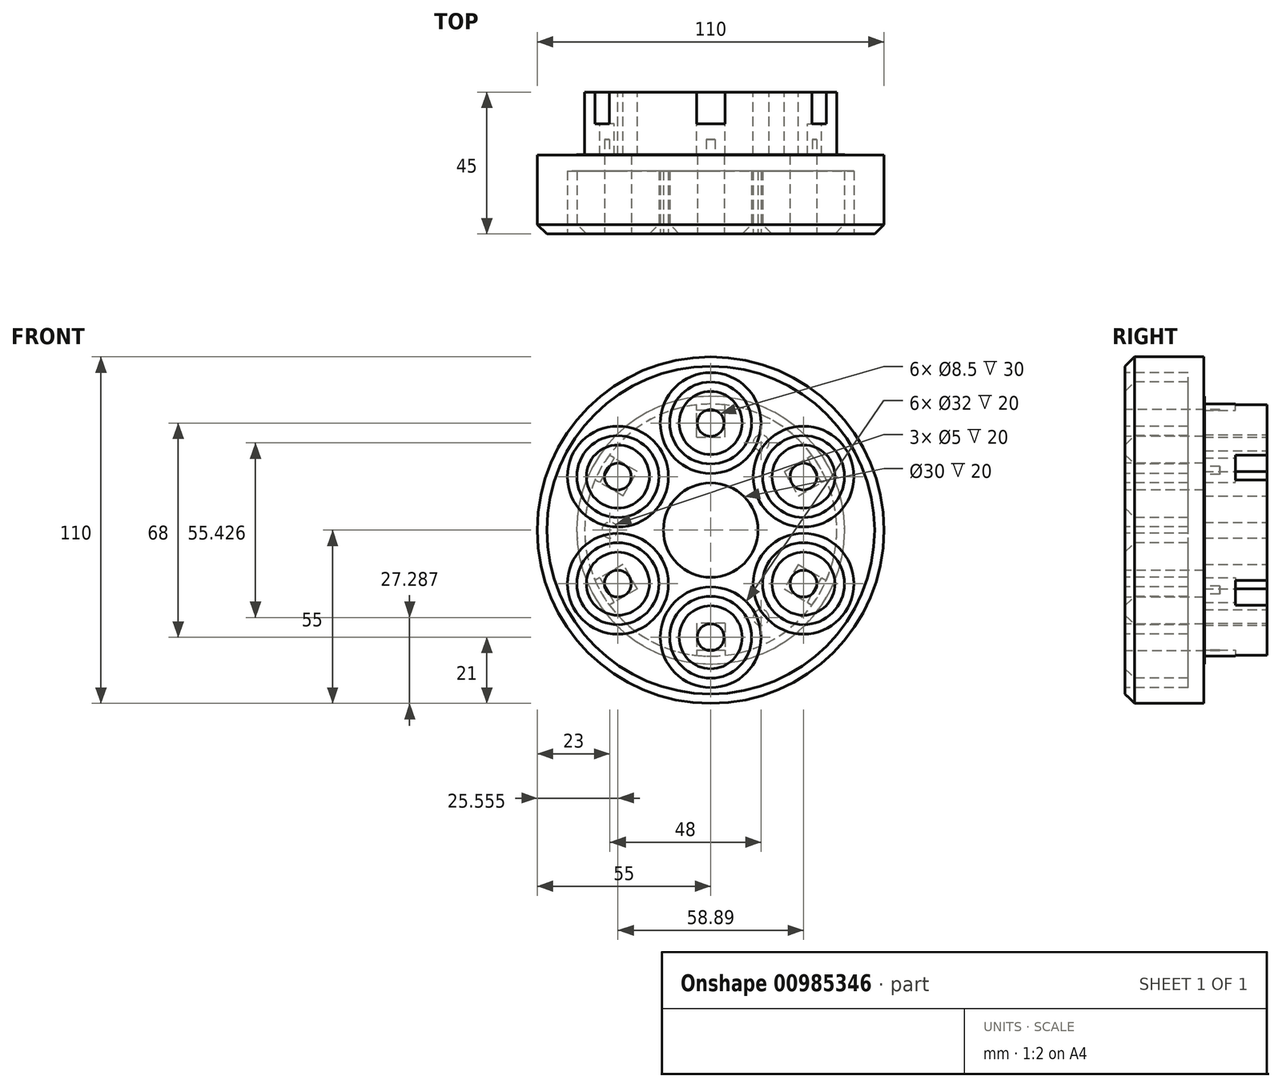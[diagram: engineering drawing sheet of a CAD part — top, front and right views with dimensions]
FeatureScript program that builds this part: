
annotation { "Feature Type Name" : "Feature", "Feature Type Description" : "" }
export const myFeature = defineFeature(function(context is Context, id is Id, definition is map)
    precondition{}
    {
        {
            var Q0;
            Q0=qCreatedBy(makeId("Front.planeOp"),FACE);
            var sketch = newSketch(context, id + "F0", { "sketchPlane" : qUnion([Q0])});
            skCircle(sketch, "E0", {"center": v(0, 0) * mm, "radius": 40 * mm});
            skCircle(sketch, "E1", {"center": v(0, 34) * mm, "radius": 3.25 * mm});
            skCircle(sketch, "E2.1.0", {"center": v(-29.44, 17) * mm, "radius": 3.25 * mm});
            skCircle(sketch, "E2.2.0", {"center": v(-29.44, -17) * mm, "radius": 3.25 * mm});
            skCircle(sketch, "E2.3.0", {"center": v(0, -34) * mm, "radius": 3.25 * mm});
            skCircle(sketch, "E2.4.0", {"center": v(29.44, -17) * mm, "radius": 3.25 * mm});
            skCircle(sketch, "E2.5.0", {"center": v(29.44, 17) * mm, "radius": 3.25 * mm});
            skSolve(sketch);
        }
        {
            var Q0;
            Q0=qSketchRegion(id+"F0",true);
            extrude(context, id + "F1", {"entities" : qUnion([Q0]), "depth" : 45 * mm});
        }
        {
            var Q0;
            Q0=makeQuery(id+"F1.opExtrude","CAP_FACE",FACE,{"disambiguationData":[OSD([sQuery(id+"F0.wireOp",EDGE,"E0"),sQuery(id+"F0.wireOp",EDGE,"E1"),sQuery(id+"F0.wireOp",EDGE,"E2.1.0"),sQuery(id+"F0.wireOp",EDGE,"E2.2.0"),sQuery(id+"F0.wireOp",EDGE,"E2.3.0"),sQuery(id+"F0.wireOp",EDGE,"E2.4.0"),sQuery(id+"F0.wireOp",EDGE,"E2.5.0")])],"isStart":false});
            var sketch = newSketch(context, id + "F2", { "sketchPlane" : qUnion([Q0])});
            skCircle(sketch, "E3", {"center": v(0, 34) * mm, "radius": 4.25 * mm});
            skCircle(sketch, "E4.1.0", {"center": v(-29.44, 17) * mm, "radius": 4.25 * mm});
            skCircle(sketch, "E4.2.0", {"center": v(-29.44, -17) * mm, "radius": 4.25 * mm});
            skCircle(sketch, "E4.3.0", {"center": v(0, -34) * mm, "radius": 4.25 * mm});
            skCircle(sketch, "E4.4.0", {"center": v(29.44, -17) * mm, "radius": 4.25 * mm});
            skCircle(sketch, "E4.5.0", {"center": v(29.44, 17) * mm, "radius": 4.25 * mm});
            skPoint(sketch, "E4.center", {"position": v(0, 0) * mm});
            skSolve(sketch);
        }
        {
            var Q0;
            Q0=qSketchRegion(id+"F2",true);
            extrude(context, id + "F3", {"entities" : qUnion([Q0]), "operationType" : NewBodyOperationType.REMOVE, "oppositeDirection" : true, "depth" : 30 * mm});
        }
        {
            var Q0;
            Q0=makeQuery(id+"F1.opExtrude","CAP_FACE",FACE,{"disambiguationData":[OSD([sQuery(id+"F0.wireOp",EDGE,"E0"),sQuery(id+"F0.wireOp",EDGE,"E1"),sQuery(id+"F0.wireOp",EDGE,"E2.1.0"),sQuery(id+"F0.wireOp",EDGE,"E2.2.0"),sQuery(id+"F0.wireOp",EDGE,"E2.3.0"),sQuery(id+"F0.wireOp",EDGE,"E2.4.0"),sQuery(id+"F0.wireOp",EDGE,"E2.5.0")])],"isStart":true});
            var sketch = newSketch(context, id + "F4", { "sketchPlane" : qUnion([Q0])});
            skCircle(sketch, "E5", {"center": v(0, 34) * mm, "radius": 4.5 * mm});
            skCircle(sketch, "E6.1.0", {"center": v(-29.44, 17) * mm, "radius": 4.5 * mm});
            skCircle(sketch, "E6.2.0", {"center": v(-29.44, -17) * mm, "radius": 4.5 * mm});
            skCircle(sketch, "E6.3.0", {"center": v(0, -34) * mm, "radius": 4.5 * mm});
            skCircle(sketch, "E6.4.0", {"center": v(29.44, -17) * mm, "radius": 4.5 * mm});
            skCircle(sketch, "E6.5.0", {"center": v(29.44, 17) * mm, "radius": 4.5 * mm});
            skPoint(sketch, "E6.center", {"position": v(0, 0) * mm});
            skCircle(sketch, "E7", {"center": v(32, 0) * mm, "radius": 2.5 * mm});
            skCircle(sketch, "E8.1.0", {"center": v(-16, 27.71) * mm, "radius": 2.5 * mm});
            skCircle(sketch, "E8.2.0", {"center": v(-16, -27.71) * mm, "radius": 2.5 * mm});
            skSolve(sketch);
        }
        {
            var Q0;
            Q0=makeQuery(id+"F4.imprint","IMPRINT",FACE,{"disambiguationData":[TD([[makeQuery(id+"F4.imprint","IMPRINT",EDGE,{"derivedFrom":sQuery(id+"F4.wireOp",EDGE,"E8.1.0")}),1.0]])]});
            var Q1;
            Q1=makeQuery(id+"F4.imprint","IMPRINT",FACE,{"disambiguationData":[TD([[makeQuery(id+"F4.imprint","IMPRINT",EDGE,{"derivedFrom":sQuery(id+"F4.wireOp",EDGE,"E7")}),1.0]])]});
            var Q2;
            Q2=makeQuery(id+"F4.imprint","IMPRINT",FACE,{"disambiguationData":[TD([[makeQuery(id+"F4.imprint","IMPRINT",EDGE,{"derivedFrom":sQuery(id+"F4.wireOp",EDGE,"E8.2.0")}),1.0]])]});
            extrude(context, id + "F5", {"entities" : qUnion([Q0, Q1, Q2]), "operationType" : NewBodyOperationType.REMOVE, "oppositeDirection" : true, "depth" : 20 * mm});
        }
        {
            var Q0;
            Q0=makeQuery(id+"F1.opExtrude","CAP_FACE",FACE,{"disambiguationData":[OSD([sQuery(id+"F0.wireOp",EDGE,"E0"),sQuery(id+"F0.wireOp",EDGE,"E1"),sQuery(id+"F0.wireOp",EDGE,"E2.1.0"),sQuery(id+"F0.wireOp",EDGE,"E2.2.0"),sQuery(id+"F0.wireOp",EDGE,"E2.3.0"),sQuery(id+"F0.wireOp",EDGE,"E2.4.0"),sQuery(id+"F0.wireOp",EDGE,"E2.5.0")])],"isStart":false});
            var sketch = newSketch(context, id + "F6", { "sketchPlane" : qUnion([Q0])});
            skCircle(sketch, "E9", {"center": v(0, 0) * mm, "radius": 55 * mm});
            skCircle(sketch, "E10", {"center": v(0, 34) * mm, "radius": 16 * mm});
            skCircle(sketch, "E11.1.0", {"center": v(-29.44, 17) * mm, "radius": 16 * mm});
            skCircle(sketch, "E11.2.0", {"center": v(-29.44, -17) * mm, "radius": 16 * mm});
            skCircle(sketch, "E11.3.0", {"center": v(0, -34) * mm, "radius": 16 * mm});
            skCircle(sketch, "E11.4.0", {"center": v(29.44, -17) * mm, "radius": 16 * mm});
            skCircle(sketch, "E11.5.0", {"center": v(29.44, 17) * mm, "radius": 16 * mm});
            skCircle(sketch, "E12", {"center": v(0, 0) * mm, "radius": 15 * mm});
            skCircle(sketch, "E13", {"center": v(0, -34) * mm, "radius": 13 * mm});
            skCircle(sketch, "E14.1.0", {"center": v(29.44, -17) * mm, "radius": 13 * mm});
            skCircle(sketch, "E14.2.0", {"center": v(29.44, 17) * mm, "radius": 13 * mm});
            skCircle(sketch, "E14.3.0", {"center": v(0, 34) * mm, "radius": 13 * mm});
            skCircle(sketch, "E14.4.0", {"center": v(-29.44, 17) * mm, "radius": 13 * mm});
            skCircle(sketch, "E14.5.0", {"center": v(-29.44, -17) * mm, "radius": 13 * mm});
            skSolve(sketch);
        }
        {
            var Q0;
            Q0=makeQuery(id+"F6.imprint","IMPRINT",FACE,{"disambiguationData":[TD([[makeQuery(id+"F6.imprint","IMPRINT",EDGE,{"derivedFrom":sQuery(id+"F6.wireOp",EDGE,"E9")}),1.0]])]});
            var Q1;
            {var subQ0=sQuery(id+"F6.wireOp",EDGE,"E11.1.0");var subQ1=makeQuery(id+"F1.opExtrude","CAP_EDGE",EDGE,{"disambiguationData":[OSD([sQuery(id+"F0.wireOp",EDGE,"E0")])],"isStart":false});var subQ2=makeQuery(id+"F6.imprint","INTERSECT",VERTEX,{"disambiguationData":[OD(0.0)],"derivedFrom":[subQ1,subQ0]});Q1=makeQuery(id+"F6.imprint","IMPRINT",FACE,{"disambiguationData":[TD([[makeQuery(id+"F6.imprint","IMPRINT",EDGE,{"disambiguationData":[TD([[subQ2,1.0]])],"derivedFrom":subQ0}),1.0]])]});}
            var Q2;
            {var subQ0=sQuery(id+"F6.wireOp",EDGE,"E10");var subQ1=makeQuery(id+"F1.opExtrude","CAP_EDGE",EDGE,{"disambiguationData":[OSD([sQuery(id+"F0.wireOp",EDGE,"E0")])],"isStart":false});var subQ2=makeQuery(id+"F6.imprint","INTERSECT",VERTEX,{"disambiguationData":[OD(0.0)],"derivedFrom":[subQ1,subQ0]});Q2=makeQuery(id+"F6.imprint","IMPRINT",FACE,{"disambiguationData":[TD([[makeQuery(id+"F6.imprint","IMPRINT",EDGE,{"disambiguationData":[TD([[subQ2,1.0]])],"derivedFrom":subQ0}),1.0]])]});}
            var Q3;
            {var subQ0=sQuery(id+"F6.wireOp",EDGE,"E11.5.0");var subQ1=makeQuery(id+"F1.opExtrude","CAP_EDGE",EDGE,{"disambiguationData":[OSD([sQuery(id+"F0.wireOp",EDGE,"E0")])],"isStart":false});var subQ2=makeQuery(id+"F6.imprint","INTERSECT",VERTEX,{"disambiguationData":[OD(0.0)],"derivedFrom":[subQ1,subQ0]});Q3=makeQuery(id+"F6.imprint","IMPRINT",FACE,{"disambiguationData":[TD([[makeQuery(id+"F6.imprint","IMPRINT",EDGE,{"disambiguationData":[TD([[subQ2,1.0]])],"derivedFrom":subQ0}),1.0]])]});}
            var Q4;
            {var subQ0=sQuery(id+"F6.wireOp",EDGE,"E11.2.0");var subQ1=makeQuery(id+"F1.opExtrude","CAP_EDGE",EDGE,{"disambiguationData":[OSD([sQuery(id+"F0.wireOp",EDGE,"E0")])],"isStart":false});var subQ2=makeQuery(id+"F6.imprint","INTERSECT",VERTEX,{"disambiguationData":[OD(0.0)],"derivedFrom":[subQ1,subQ0]});Q4=makeQuery(id+"F6.imprint","IMPRINT",FACE,{"disambiguationData":[TD([[makeQuery(id+"F6.imprint","IMPRINT",EDGE,{"disambiguationData":[TD([[subQ2,-1.0]])],"derivedFrom":subQ0}),1.0]])]});}
            var Q5;
            {var subQ0=sQuery(id+"F6.wireOp",EDGE,"E11.3.0");var subQ1=makeQuery(id+"F1.opExtrude","CAP_EDGE",EDGE,{"disambiguationData":[OSD([sQuery(id+"F0.wireOp",EDGE,"E0")])],"isStart":false});var subQ2=makeQuery(id+"F6.imprint","INTERSECT",VERTEX,{"disambiguationData":[OD(0.0)],"derivedFrom":[subQ1,subQ0]});Q5=makeQuery(id+"F6.imprint","IMPRINT",FACE,{"disambiguationData":[TD([[makeQuery(id+"F6.imprint","IMPRINT",EDGE,{"disambiguationData":[TD([[subQ2,-1.0]])],"derivedFrom":subQ0}),1.0]])]});}
            var Q6;
            {var subQ0=sQuery(id+"F6.wireOp",EDGE,"E11.4.0");var subQ1=makeQuery(id+"F1.opExtrude","CAP_EDGE",EDGE,{"disambiguationData":[OSD([sQuery(id+"F0.wireOp",EDGE,"E0")])],"isStart":false});var subQ2=makeQuery(id+"F6.imprint","INTERSECT",VERTEX,{"disambiguationData":[OD(0.0)],"derivedFrom":[subQ1,subQ0]});Q6=makeQuery(id+"F6.imprint","IMPRINT",FACE,{"disambiguationData":[TD([[makeQuery(id+"F6.imprint","IMPRINT",EDGE,{"disambiguationData":[TD([[subQ2,-1.0]])],"derivedFrom":subQ0}),1.0]])]});}
            var Q7;
            {var subQ0=sQuery(id+"F6.wireOp",EDGE,"E14.5.0");var subQ1=makeQuery(id+"F1.opExtrude","CAP_EDGE",EDGE,{"disambiguationData":[OSD([sQuery(id+"F0.wireOp",EDGE,"E0")])],"isStart":false});var subQ2=makeQuery(id+"F6.imprint","INTERSECT",VERTEX,{"disambiguationData":[OD(0.0)],"derivedFrom":[subQ1,subQ0]});Q7=makeQuery(id+"F6.imprint","IMPRINT",FACE,{"disambiguationData":[TD([[makeQuery(id+"F6.imprint","IMPRINT",EDGE,{"disambiguationData":[TD([[subQ2,-1.0]])],"derivedFrom":subQ0}),1.0]])]});}
            var Q8;
            {var subQ0=sQuery(id+"F6.wireOp",EDGE,"E14.4.0");var subQ1=makeQuery(id+"F1.opExtrude","CAP_EDGE",EDGE,{"disambiguationData":[OSD([sQuery(id+"F0.wireOp",EDGE,"E0")])],"isStart":false});var subQ2=makeQuery(id+"F6.imprint","INTERSECT",VERTEX,{"disambiguationData":[OD(0.0)],"derivedFrom":[subQ1,subQ0]});Q8=makeQuery(id+"F6.imprint","IMPRINT",FACE,{"disambiguationData":[TD([[makeQuery(id+"F6.imprint","IMPRINT",EDGE,{"disambiguationData":[TD([[subQ2,1.0]])],"derivedFrom":subQ0}),1.0]])]});}
            var Q9;
            {var subQ0=sQuery(id+"F6.wireOp",EDGE,"E14.3.0");var subQ1=makeQuery(id+"F1.opExtrude","CAP_EDGE",EDGE,{"disambiguationData":[OSD([sQuery(id+"F0.wireOp",EDGE,"E0")])],"isStart":false});var subQ2=makeQuery(id+"F6.imprint","INTERSECT",VERTEX,{"disambiguationData":[OD(0.0)],"derivedFrom":[subQ1,subQ0]});Q9=makeQuery(id+"F6.imprint","IMPRINT",FACE,{"disambiguationData":[TD([[makeQuery(id+"F6.imprint","IMPRINT",EDGE,{"disambiguationData":[TD([[subQ2,1.0]])],"derivedFrom":subQ0}),1.0]])]});}
            var Q10;
            {var subQ0=sQuery(id+"F6.wireOp",EDGE,"E14.2.0");var subQ1=makeQuery(id+"F1.opExtrude","CAP_EDGE",EDGE,{"disambiguationData":[OSD([sQuery(id+"F0.wireOp",EDGE,"E0")])],"isStart":false});var subQ2=makeQuery(id+"F6.imprint","INTERSECT",VERTEX,{"disambiguationData":[OD(0.0)],"derivedFrom":[subQ1,subQ0]});Q10=makeQuery(id+"F6.imprint","IMPRINT",FACE,{"disambiguationData":[TD([[makeQuery(id+"F6.imprint","IMPRINT",EDGE,{"disambiguationData":[TD([[subQ2,1.0]])],"derivedFrom":subQ0}),1.0]])]});}
            var Q11;
            {var subQ0=sQuery(id+"F6.wireOp",EDGE,"E14.1.0");var subQ1=makeQuery(id+"F1.opExtrude","CAP_EDGE",EDGE,{"disambiguationData":[OSD([sQuery(id+"F0.wireOp",EDGE,"E0")])],"isStart":false});var subQ2=makeQuery(id+"F6.imprint","INTERSECT",VERTEX,{"disambiguationData":[OD(0.0)],"derivedFrom":[subQ1,subQ0]});Q11=makeQuery(id+"F6.imprint","IMPRINT",FACE,{"disambiguationData":[TD([[makeQuery(id+"F6.imprint","IMPRINT",EDGE,{"disambiguationData":[TD([[subQ2,-1.0]])],"derivedFrom":subQ0}),1.0]])]});}
            var Q12;
            {var subQ0=sQuery(id+"F6.wireOp",EDGE,"E13");var subQ1=makeQuery(id+"F1.opExtrude","CAP_EDGE",EDGE,{"disambiguationData":[OSD([sQuery(id+"F0.wireOp",EDGE,"E0")])],"isStart":false});var subQ2=makeQuery(id+"F6.imprint","INTERSECT",VERTEX,{"disambiguationData":[OD(0.0)],"derivedFrom":[subQ1,subQ0]});Q12=makeQuery(id+"F6.imprint","IMPRINT",FACE,{"disambiguationData":[TD([[makeQuery(id+"F6.imprint","IMPRINT",EDGE,{"disambiguationData":[TD([[subQ2,-1.0]])],"derivedFrom":subQ0}),1.0]])]});}
            extrude(context, id + "F7", {"entities" : qUnion([Q0, Q1, Q2, Q3, Q4, Q5, Q6, Q7, Q8, Q9, Q10, Q11, Q12]), "operationType" : NewBodyOperationType.ADD, "oppositeDirection" : true, "depth" : 25 * mm});
        }
        {
            var Q0;
            {var subQ0=sQuery(id+"F6.wireOp",EDGE,"E11.3.0");var subQ1=makeQuery(id+"F1.opExtrude","CAP_EDGE",EDGE,{"disambiguationData":[OSD([sQuery(id+"F0.wireOp",EDGE,"E0")])],"isStart":false});var subQ2=makeQuery(id+"F6.imprint","INTERSECT",VERTEX,{"disambiguationData":[OD(0.0)],"derivedFrom":[subQ1,subQ0]});Q0=makeQuery(id+"F6.imprint","IMPRINT",FACE,{"disambiguationData":[TD([[makeQuery(id+"F6.imprint","IMPRINT",EDGE,{"disambiguationData":[TD([[subQ2,-1.0]])],"derivedFrom":subQ0}),1.0]])]});}
            var Q1;
            {var subQ0=sQuery(id+"F6.wireOp",EDGE,"E11.4.0");var subQ1=makeQuery(id+"F1.opExtrude","CAP_EDGE",EDGE,{"disambiguationData":[OSD([sQuery(id+"F0.wireOp",EDGE,"E0")])],"isStart":false});var subQ2=makeQuery(id+"F6.imprint","INTERSECT",VERTEX,{"disambiguationData":[OD(0.0)],"derivedFrom":[subQ1,subQ0]});Q1=makeQuery(id+"F6.imprint","IMPRINT",FACE,{"disambiguationData":[TD([[makeQuery(id+"F6.imprint","IMPRINT",EDGE,{"disambiguationData":[TD([[subQ2,-1.0]])],"derivedFrom":subQ0}),1.0]])]});}
            var Q2;
            {var subQ0=sQuery(id+"F6.wireOp",EDGE,"E11.5.0");var subQ1=makeQuery(id+"F1.opExtrude","CAP_EDGE",EDGE,{"disambiguationData":[OSD([sQuery(id+"F0.wireOp",EDGE,"E0")])],"isStart":false});var subQ2=makeQuery(id+"F6.imprint","INTERSECT",VERTEX,{"disambiguationData":[OD(0.0)],"derivedFrom":[subQ1,subQ0]});Q2=makeQuery(id+"F6.imprint","IMPRINT",FACE,{"disambiguationData":[TD([[makeQuery(id+"F6.imprint","IMPRINT",EDGE,{"disambiguationData":[TD([[subQ2,1.0]])],"derivedFrom":subQ0}),1.0]])]});}
            var Q3;
            {var subQ0=sQuery(id+"F6.wireOp",EDGE,"E11.1.0");var subQ1=makeQuery(id+"F1.opExtrude","CAP_EDGE",EDGE,{"disambiguationData":[OSD([sQuery(id+"F0.wireOp",EDGE,"E0")])],"isStart":false});var subQ2=makeQuery(id+"F6.imprint","INTERSECT",VERTEX,{"disambiguationData":[OD(0.0)],"derivedFrom":[subQ1,subQ0]});Q3=makeQuery(id+"F6.imprint","IMPRINT",FACE,{"disambiguationData":[TD([[makeQuery(id+"F6.imprint","IMPRINT",EDGE,{"disambiguationData":[TD([[subQ2,1.0]])],"derivedFrom":subQ0}),1.0]])]});}
            var Q4;
            {var subQ0=sQuery(id+"F6.wireOp",EDGE,"E10");var subQ1=makeQuery(id+"F1.opExtrude","CAP_EDGE",EDGE,{"disambiguationData":[OSD([sQuery(id+"F0.wireOp",EDGE,"E0")])],"isStart":false});var subQ2=makeQuery(id+"F6.imprint","INTERSECT",VERTEX,{"disambiguationData":[OD(0.0)],"derivedFrom":[subQ1,subQ0]});Q4=makeQuery(id+"F6.imprint","IMPRINT",FACE,{"disambiguationData":[TD([[makeQuery(id+"F6.imprint","IMPRINT",EDGE,{"disambiguationData":[TD([[subQ2,1.0]])],"derivedFrom":subQ0}),1.0]])]});}
            var Q5;
            Q5=makeQuery(id+"F6.imprint","IMPRINT",FACE,{"disambiguationData":[TD([[makeQuery(id+"F6.imprint","IMPRINT",EDGE,{"derivedFrom":sQuery(id+"F6.wireOp",EDGE,"E12")}),1.0]])]});
            var Q6;
            {var subQ0=sQuery(id+"F6.wireOp",EDGE,"E11.1.0");var subQ1=makeQuery(id+"F1.opExtrude","CAP_EDGE",EDGE,{"disambiguationData":[OSD([sQuery(id+"F0.wireOp",EDGE,"E0")])],"isStart":false});var subQ2=makeQuery(id+"F6.imprint","INTERSECT",VERTEX,{"disambiguationData":[OD(0.0)],"derivedFrom":[subQ1,subQ0]});Q6=makeQuery(id+"F6.imprint","IMPRINT",FACE,{"disambiguationData":[TD([[makeQuery(id+"F6.imprint","IMPRINT",EDGE,{"disambiguationData":[TD([[subQ2,-1.0]])],"derivedFrom":subQ0}),1.0]])]});}
            var Q7;
            {var subQ0=sQuery(id+"F6.wireOp",EDGE,"E11.2.0");var subQ1=makeQuery(id+"F1.opExtrude","CAP_EDGE",EDGE,{"disambiguationData":[OSD([sQuery(id+"F0.wireOp",EDGE,"E0")])],"isStart":false});var subQ2=makeQuery(id+"F6.imprint","INTERSECT",VERTEX,{"disambiguationData":[OD(0.0)],"derivedFrom":[subQ1,subQ0]});Q7=makeQuery(id+"F6.imprint","IMPRINT",FACE,{"disambiguationData":[TD([[makeQuery(id+"F6.imprint","IMPRINT",EDGE,{"disambiguationData":[TD([[subQ2,1.0]])],"derivedFrom":subQ0}),1.0]])]});}
            var Q8;
            {var subQ0=sQuery(id+"F6.wireOp",EDGE,"E11.2.0");var subQ1=makeQuery(id+"F1.opExtrude","CAP_EDGE",EDGE,{"disambiguationData":[OSD([sQuery(id+"F0.wireOp",EDGE,"E0")])],"isStart":false});var subQ2=makeQuery(id+"F6.imprint","INTERSECT",VERTEX,{"disambiguationData":[OD(0.0)],"derivedFrom":[subQ1,subQ0]});Q8=makeQuery(id+"F6.imprint","IMPRINT",FACE,{"disambiguationData":[TD([[makeQuery(id+"F6.imprint","IMPRINT",EDGE,{"disambiguationData":[TD([[subQ2,-1.0]])],"derivedFrom":subQ0}),1.0]])]});}
            var Q9;
            {var subQ0=sQuery(id+"F6.wireOp",EDGE,"E10");var subQ1=makeQuery(id+"F1.opExtrude","CAP_EDGE",EDGE,{"disambiguationData":[OSD([sQuery(id+"F0.wireOp",EDGE,"E0")])],"isStart":false});var subQ2=makeQuery(id+"F6.imprint","INTERSECT",VERTEX,{"disambiguationData":[OD(0.0)],"derivedFrom":[subQ1,subQ0]});Q9=makeQuery(id+"F6.imprint","IMPRINT",FACE,{"disambiguationData":[TD([[makeQuery(id+"F6.imprint","IMPRINT",EDGE,{"disambiguationData":[TD([[subQ2,-1.0]])],"derivedFrom":subQ0}),1.0]])]});}
            var Q10;
            {var subQ0=sQuery(id+"F6.wireOp",EDGE,"E11.5.0");var subQ1=makeQuery(id+"F1.opExtrude","CAP_EDGE",EDGE,{"disambiguationData":[OSD([sQuery(id+"F0.wireOp",EDGE,"E0")])],"isStart":false});var subQ2=makeQuery(id+"F6.imprint","INTERSECT",VERTEX,{"disambiguationData":[OD(0.0)],"derivedFrom":[subQ1,subQ0]});Q10=makeQuery(id+"F6.imprint","IMPRINT",FACE,{"disambiguationData":[TD([[makeQuery(id+"F6.imprint","IMPRINT",EDGE,{"disambiguationData":[TD([[subQ2,-1.0]])],"derivedFrom":subQ0}),1.0]])]});}
            var Q11;
            {var subQ0=sQuery(id+"F6.wireOp",EDGE,"E11.4.0");var subQ1=makeQuery(id+"F1.opExtrude","CAP_EDGE",EDGE,{"disambiguationData":[OSD([sQuery(id+"F0.wireOp",EDGE,"E0")])],"isStart":false});var subQ2=makeQuery(id+"F6.imprint","INTERSECT",VERTEX,{"disambiguationData":[OD(0.0)],"derivedFrom":[subQ1,subQ0]});Q11=makeQuery(id+"F6.imprint","IMPRINT",FACE,{"disambiguationData":[TD([[makeQuery(id+"F6.imprint","IMPRINT",EDGE,{"disambiguationData":[TD([[subQ2,1.0]])],"derivedFrom":subQ0}),1.0]])]});}
            var Q12;
            {var subQ0=sQuery(id+"F6.wireOp",EDGE,"E11.3.0");var subQ1=makeQuery(id+"F1.opExtrude","CAP_EDGE",EDGE,{"disambiguationData":[OSD([sQuery(id+"F0.wireOp",EDGE,"E0")])],"isStart":false});var subQ2=makeQuery(id+"F6.imprint","INTERSECT",VERTEX,{"disambiguationData":[OD(0.0)],"derivedFrom":[subQ1,subQ0]});Q12=makeQuery(id+"F6.imprint","IMPRINT",FACE,{"disambiguationData":[TD([[makeQuery(id+"F6.imprint","IMPRINT",EDGE,{"disambiguationData":[TD([[subQ2,1.0]])],"derivedFrom":subQ0}),1.0]])]});}
            extrude(context, id + "F8", {"entities" : qUnion([Q0, Q1, Q2, Q3, Q4, Q5, Q6, Q7, Q8, Q9, Q10, Q11, Q12]), "operationType" : NewBodyOperationType.REMOVE, "oppositeDirection" : true, "depth" : 20 * mm});
        }
        {
            var Q0;
            Q0=makeQuery(id+"F7.opExtrude","CAP_EDGE",EDGE,{"disambiguationData":[OSD([sQuery(id+"F6.wireOp",EDGE,"E9")])],"isStart":true});
            var Q1;
            Q1=makeQuery(id+"F8.boolean.opBoolean","COPY",EDGE,{"derivedFrom":makeQuery(id+"F8.opExtrude","CAP_EDGE",EDGE,{"disambiguationData":[OSD([sQuery(id+"F6.wireOp",EDGE,"E14.4.0")])],"isStart":true})});
            var Q2;
            Q2=makeQuery(id+"F8.boolean.opBoolean","COPY",EDGE,{"derivedFrom":makeQuery(id+"F8.opExtrude","CAP_EDGE",EDGE,{"disambiguationData":[OSD([sQuery(id+"F6.wireOp",EDGE,"E14.3.0")])],"isStart":true})});
            var Q3;
            Q3=makeQuery(id+"F8.boolean.opBoolean","COPY",EDGE,{"derivedFrom":makeQuery(id+"F8.opExtrude","CAP_EDGE",EDGE,{"disambiguationData":[OSD([sQuery(id+"F6.wireOp",EDGE,"E14.2.0")])],"isStart":true})});
            var Q4;
            Q4=makeQuery(id+"F8.boolean.opBoolean","COPY",EDGE,{"derivedFrom":makeQuery(id+"F8.opExtrude","CAP_EDGE",EDGE,{"disambiguationData":[OSD([sQuery(id+"F6.wireOp",EDGE,"E14.1.0")])],"isStart":true})});
            var Q5;
            Q5=makeQuery(id+"F8.boolean.opBoolean","COPY",EDGE,{"derivedFrom":makeQuery(id+"F8.opExtrude","CAP_EDGE",EDGE,{"disambiguationData":[OSD([sQuery(id+"F6.wireOp",EDGE,"E13")])],"isStart":true})});
            var Q6;
            Q6=makeQuery(id+"F8.boolean.opBoolean","COPY",EDGE,{"derivedFrom":makeQuery(id+"F8.opExtrude","CAP_EDGE",EDGE,{"disambiguationData":[OSD([sQuery(id+"F6.wireOp",EDGE,"E14.5.0")])],"isStart":true})});
            chamfer(context, id + "F9", {"entities" : qUnion([Q0, Q1, Q2, Q3, Q4, Q5, Q6]), "width" : 3 * mm, "tangentPropagation" : true});
        }
        {
            var Q0;
            Q0=makeQuery(id+"F7.opExtrude","CAP_FACE",FACE,{"disambiguationData":[OSD([sQuery(id+"F0.wireOp",EDGE,"E0"),sQuery(id+"F6.wireOp",EDGE,"E9")])],"isStart":false});
            var sketch = newSketch(context, id + "F10", { "sketchPlane" : qUnion([Q0])});
            skCircle(sketch, "E15", {"center": v(0, 0) * mm, "radius": 42.5 * mm});
            skSolve(sketch);
        }
        {
            var Q0;
            Q0=makeQuery(id+"F10.imprint","IMPRINT",FACE,{"disambiguationData":[TD([[makeQuery(id+"F10.imprint","IMPRINT",EDGE,{"derivedFrom":sQuery(id+"F10.wireOp",EDGE,"E15")}),1.0]])]});
            extrude(context, id + "F11", {"entities" : qUnion([Q0]), "operationType" : NewBodyOperationType.ADD, "depth" : 0.2 * mm});
        }
        {
            var Q0;
            Q0=makeQuery(id+"F1.opExtrude","CAP_FACE",FACE,{"disambiguationData":[OSD([sQuery(id+"F0.wireOp",EDGE,"E0"),sQuery(id+"F0.wireOp",EDGE,"E1"),sQuery(id+"F0.wireOp",EDGE,"E2.1.0"),sQuery(id+"F0.wireOp",EDGE,"E2.2.0"),sQuery(id+"F0.wireOp",EDGE,"E2.3.0"),sQuery(id+"F0.wireOp",EDGE,"E2.4.0"),sQuery(id+"F0.wireOp",EDGE,"E2.5.0")])],"isStart":true});
            var sketch = newSketch(context, id + "F12", { "sketchPlane" : qUnion([Q0])});
            skLineSegment(sketch, "E16.bottom", {"start": v(4.5, 29.5) * mm, "end": v(-4.5, 29.5) * mm});
            skLineSegment(sketch, "E16.left", {"start": v(4.5, 29.5) * mm, "end": v(4.5, 39.75) * mm});
            skLineSegment(sketch, "E16.right", {"start": v(-4.5, 29.5) * mm, "end": v(-4.5, 39.75) * mm});
            skPoint(sketch, "E16.middle", {"position": v(0, 34) * mm});
            skArc(sketch, "E17.0", {"start": v(4.5, 39.75) * mm, "mid": v(0, 40) * mm, "end": v(-4.5, 39.75) * mm});
            skLineSegment(sketch, "E18.1.0", {"start": v(-27.8, 10.85) * mm, "end": v(-36.67, 15.98) * mm});
            skPoint(sketch, "E18.1.1", {"position": v(-29.44, 17) * mm});
            skLineSegment(sketch, "E18.1.2", {"start": v(-23.3, 18.65) * mm, "end": v(-32.17, 23.77) * mm});
            skArc(sketch, "E18.1.3", {"start": v(-32.17, 23.77) * mm, "mid": v(-34.64, 20) * mm, "end": v(-36.67, 15.98) * mm});
            skLineSegment(sketch, "E18.1.4", {"start": v(-23.3, 18.65) * mm, "end": v(-27.8, 10.85) * mm});
            skLineSegment(sketch, "E18.2.0", {"start": v(-23.3, -18.65) * mm, "end": v(-32.17, -23.77) * mm});
            skPoint(sketch, "E18.2.1", {"position": v(-29.44, -17) * mm});
            skLineSegment(sketch, "E18.2.2", {"start": v(-27.8, -10.85) * mm, "end": v(-36.67, -15.98) * mm});
            skArc(sketch, "E18.2.3", {"start": v(-36.67, -15.98) * mm, "mid": v(-34.64, -20) * mm, "end": v(-32.17, -23.77) * mm});
            skLineSegment(sketch, "E18.2.4", {"start": v(-27.8, -10.85) * mm, "end": v(-23.3, -18.65) * mm});
            skLineSegment(sketch, "E18.3.0", {"start": v(4.5, -29.5) * mm, "end": v(4.5, -39.75) * mm});
            skPoint(sketch, "E18.3.1", {"position": v(0, -34) * mm});
            skLineSegment(sketch, "E18.3.2", {"start": v(-4.5, -29.5) * mm, "end": v(-4.5, -39.75) * mm});
            skArc(sketch, "E18.3.3", {"start": v(-4.5, -39.75) * mm, "mid": v(0, -40) * mm, "end": v(4.5, -39.75) * mm});
            skLineSegment(sketch, "E18.3.4", {"start": v(-4.5, -29.5) * mm, "end": v(4.5, -29.5) * mm});
            skLineSegment(sketch, "E18.4.0", {"start": v(27.8, -10.85) * mm, "end": v(36.67, -15.98) * mm});
            skPoint(sketch, "E18.4.1", {"position": v(29.44, -17) * mm});
            skLineSegment(sketch, "E18.4.2", {"start": v(23.3, -18.65) * mm, "end": v(32.17, -23.77) * mm});
            skArc(sketch, "E18.4.3", {"start": v(32.17, -23.77) * mm, "mid": v(34.64, -20) * mm, "end": v(36.67, -15.98) * mm});
            skLineSegment(sketch, "E18.4.4", {"start": v(23.3, -18.65) * mm, "end": v(27.8, -10.85) * mm});
            skLineSegment(sketch, "E18.5.0", {"start": v(23.3, 18.65) * mm, "end": v(32.17, 23.77) * mm});
            skPoint(sketch, "E18.5.1", {"position": v(29.44, 17) * mm});
            skLineSegment(sketch, "E18.5.2", {"start": v(27.8, 10.85) * mm, "end": v(36.67, 15.98) * mm});
            skArc(sketch, "E18.5.3", {"start": v(36.67, 15.98) * mm, "mid": v(34.64, 20) * mm, "end": v(32.17, 23.77) * mm});
            skLineSegment(sketch, "E18.5.4", {"start": v(27.8, 10.85) * mm, "end": v(23.3, 18.65) * mm});
            skSolve(sketch);
        }
        {
            var Q0;
            Q0=makeQuery(id+"F12.imprint","IMPRINT",FACE,{"disambiguationData":[TD([[makeQuery(id+"F12.imprint","IMPRINT",EDGE,{"derivedFrom":sQuery(id+"F12.wireOp",EDGE,"E18.1.0")}),-1.0]])]});
            var Q1;
            Q1=makeQuery(id+"F12.imprint","IMPRINT",FACE,{"disambiguationData":[TD([[makeQuery(id+"F12.imprint","IMPRINT",EDGE,{"derivedFrom":sQuery(id+"F12.wireOp",EDGE,"E16.bottom")}),-1.0]])]});
            var Q2;
            Q2=makeQuery(id+"F12.imprint","IMPRINT",FACE,{"disambiguationData":[TD([[makeQuery(id+"F12.imprint","IMPRINT",EDGE,{"derivedFrom":sQuery(id+"F12.wireOp",EDGE,"E18.5.0")}),-1.0]])]});
            var Q3;
            Q3=makeQuery(id+"F12.imprint","IMPRINT",FACE,{"disambiguationData":[TD([[makeQuery(id+"F12.imprint","IMPRINT",EDGE,{"derivedFrom":sQuery(id+"F12.wireOp",EDGE,"E18.4.0")}),-1.0]])]});
            var Q4;
            Q4=makeQuery(id+"F12.imprint","IMPRINT",FACE,{"disambiguationData":[TD([[makeQuery(id+"F12.imprint","IMPRINT",EDGE,{"derivedFrom":sQuery(id+"F12.wireOp",EDGE,"E18.2.0")}),-1.0]])]});
            var Q5;
            Q5=makeQuery(id+"F12.imprint","IMPRINT",FACE,{"disambiguationData":[TD([[makeQuery(id+"F12.imprint","IMPRINT",EDGE,{"derivedFrom":sQuery(id+"F12.wireOp",EDGE,"E18.3.0")}),-1.0]])]});
            extrude(context, id + "F13", {"entities" : qUnion([Q0, Q1, Q2, Q3, Q4, Q5]), "operationType" : NewBodyOperationType.REMOVE, "oppositeDirection" : true, "depth" : 10 * mm});
        }
        {
            var Q0;
            Q0=makeQuery(id+"F13.boolean.opBoolean","COPY",FACE,{"derivedFrom":makeQuery(id+"F13.opExtrude","CAP_FACE",FACE,{"disambiguationData":[OSD([sQuery(id+"F0.wireOp",EDGE,"E1"),sQuery(id+"F12.wireOp",EDGE,"E16.bottom"),sQuery(id+"F12.wireOp",EDGE,"E16.left"),sQuery(id+"F12.wireOp",EDGE,"E16.right"),sQuery(id+"F12.wireOp",EDGE,"E17.0")])],"isStart":false})});
            var sketch = newSketch(context, id + "F14", { "sketchPlane" : qUnion([Q0])});
            skLineSegment(sketch, "E19.0", {"start": v(4.5, 29.5) * mm, "end": v(-4.5, 29.5) * mm});
            skLineSegment(sketch, "E19.1", {"start": v(-4.5, 29.5) * mm, "end": v(-4.5, 38) * mm});
            skLineSegment(sketch, "E19.2", {"start": v(4.5, 29.5) * mm, "end": v(4.5, 38) * mm});
            skLineSegment(sketch, "E20", {"start": v(-4.5, 38) * mm, "end": v(4.5, 38) * mm});
            skPoint(sketch, "E21.orphan", {"position": v(-4.5, 39.75) * mm});
            skPoint(sketch, "E22.orphan", {"position": v(4.5, 39.75) * mm});
            skLineSegment(sketch, "E23.1.0", {"start": v(-27.8, 10.85) * mm, "end": v(-35.16, 15.1) * mm});
            skLineSegment(sketch, "E23.1.1", {"start": v(-23.3, 18.65) * mm, "end": v(-30.66, 22.9) * mm});
            skLineSegment(sketch, "E23.1.2", {"start": v(-23.3, 18.65) * mm, "end": v(-27.8, 10.85) * mm});
            skLineSegment(sketch, "E23.1.3", {"start": v(-35.16, 15.1) * mm, "end": v(-30.66, 22.9) * mm});
            skLineSegment(sketch, "E23.2.0", {"start": v(-23.3, -18.65) * mm, "end": v(-30.66, -22.9) * mm});
            skLineSegment(sketch, "E23.2.1", {"start": v(-27.8, -10.85) * mm, "end": v(-35.16, -15.1) * mm});
            skLineSegment(sketch, "E23.2.2", {"start": v(-27.8, -10.85) * mm, "end": v(-23.3, -18.65) * mm});
            skLineSegment(sketch, "E23.2.3", {"start": v(-30.66, -22.9) * mm, "end": v(-35.16, -15.1) * mm});
            skLineSegment(sketch, "E23.3.0", {"start": v(4.5, -29.5) * mm, "end": v(4.5, -38) * mm});
            skLineSegment(sketch, "E23.3.1", {"start": v(-4.5, -29.5) * mm, "end": v(-4.5, -38) * mm});
            skLineSegment(sketch, "E23.3.2", {"start": v(-4.5, -29.5) * mm, "end": v(4.5, -29.5) * mm});
            skLineSegment(sketch, "E23.3.3", {"start": v(4.5, -38) * mm, "end": v(-4.5, -38) * mm});
            skLineSegment(sketch, "E23.4.0", {"start": v(27.8, -10.85) * mm, "end": v(35.16, -15.1) * mm});
            skLineSegment(sketch, "E23.4.1", {"start": v(23.3, -18.65) * mm, "end": v(30.66, -22.9) * mm});
            skLineSegment(sketch, "E23.4.2", {"start": v(23.3, -18.65) * mm, "end": v(27.8, -10.85) * mm});
            skLineSegment(sketch, "E23.4.3", {"start": v(35.16, -15.1) * mm, "end": v(30.66, -22.9) * mm});
            skLineSegment(sketch, "E23.5.0", {"start": v(23.3, 18.65) * mm, "end": v(30.66, 22.9) * mm});
            skLineSegment(sketch, "E23.5.1", {"start": v(27.8, 10.85) * mm, "end": v(35.16, 15.1) * mm});
            skLineSegment(sketch, "E23.5.2", {"start": v(27.8, 10.85) * mm, "end": v(23.3, 18.65) * mm});
            skLineSegment(sketch, "E23.5.3", {"start": v(30.66, 22.9) * mm, "end": v(35.16, 15.1) * mm});
            skPoint(sketch, "E23.center", {"position": v(0, 0) * mm});
            skSolve(sketch);
        }
        {
            var Q0;
            Q0=qSketchRegion(id+"F14",true);
            extrude(context, id + "F15", {"entities" : qUnion([Q0]), "operationType" : NewBodyOperationType.REMOVE, "oppositeDirection" : true, "depth" : 10 * mm});
        }
    });
